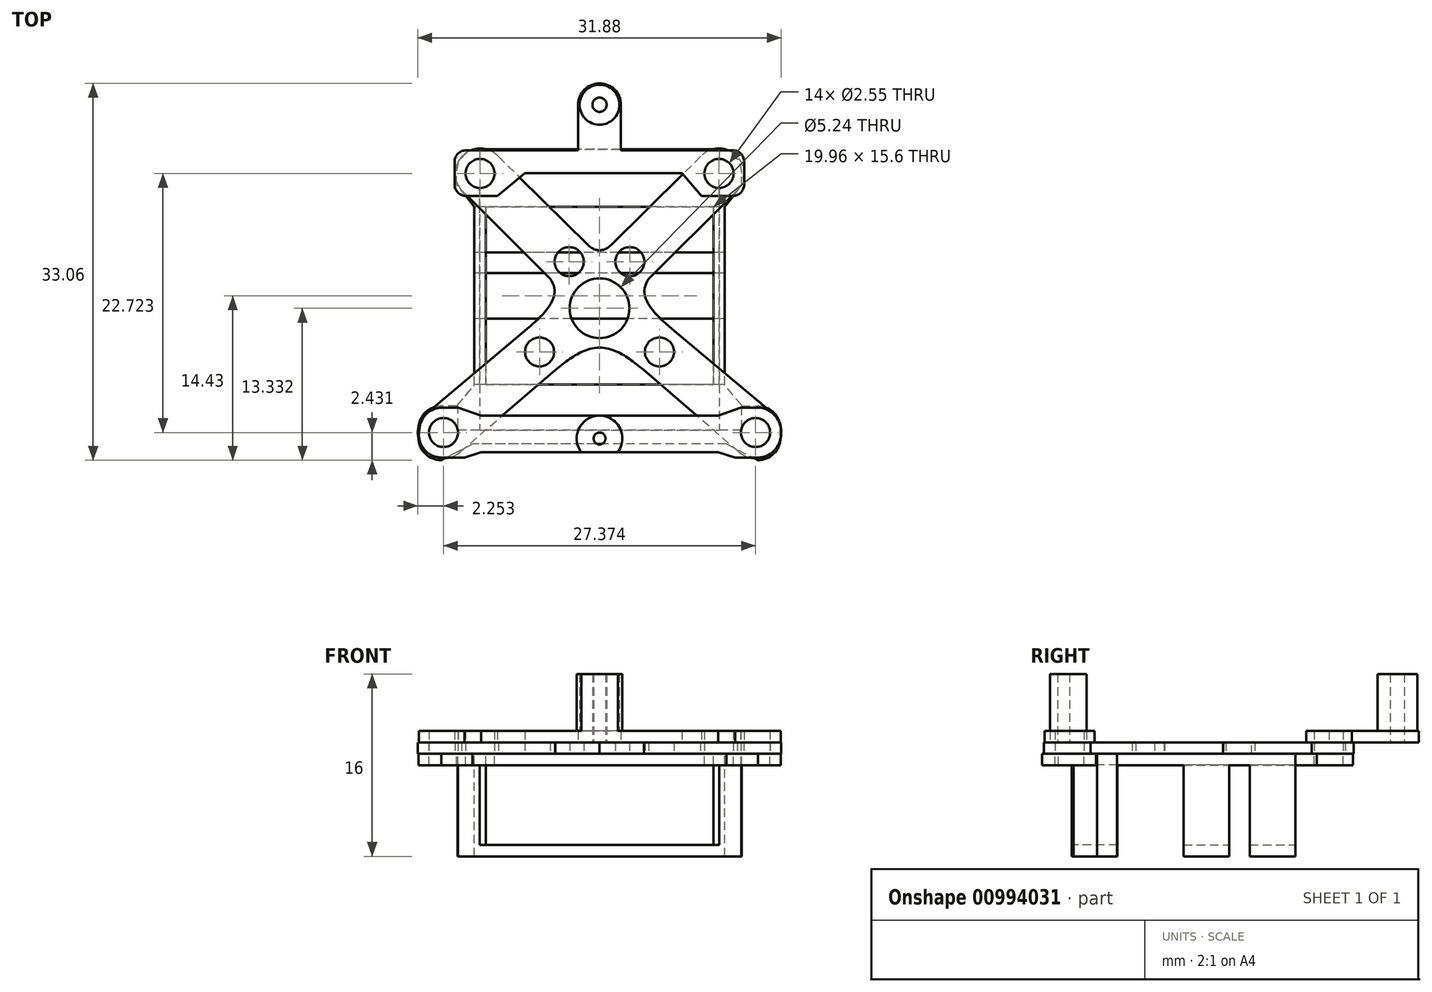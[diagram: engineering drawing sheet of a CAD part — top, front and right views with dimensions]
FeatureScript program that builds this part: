
annotation { "Feature Type Name" : "Feature", "Feature Type Description" : "" }
export const myFeature = defineFeature(function(context is Context, id is Id, definition is map)
    precondition{}
    {
        {
            var Q0;
            Q0=qCreatedBy(makeId("Top.planeOp"),FACE);
            var sketch = newSketch(context, id + "F0", { "sketchPlane" : qUnion([Q0])});
            skPoint(sketch, "E0.MirrorCS.start.orphan", {"position": v(0, 0) * mm});
            skCircle(sketch, "E1", {"center": v(-10.48, 10.72) * mm, "radius": 1.27 * mm});
            skCircle(sketch, "E2", {"center": v(-2.66, 2.99) * mm, "radius": 1.27 * mm});
            skCircle(sketch, "E3", {"center": v(-5.26, -4.93) * mm, "radius": 1.27 * mm});
            skCircle(sketch, "E4", {"center": v(-13.69, -12) * mm, "radius": 1.27 * mm});
            skLineSegment(sketch, "E5", {"start": v(-8.86, 12.2) * mm, "end": v(-1.03, 4.48) * mm});
            skLineSegment(sketch, "E6", {"start": v(-12.1, 9.24) * mm, "end": v(-4.32, 1.47) * mm});
            skArc(sketch, "E7", {"start": v(-8.86, 12.2) * mm, "mid": v(-11.96, 12.34) * mm, "end": v(-12.1, 9.24) * mm});
            skLineSegment(sketch, "E8.trimOffspring", {"start": v(-8.86, 12.2) * mm, "end": v(-8.86, 12.2) * mm});
            skLineSegment(sketch, "E9.trimOffspring", {"start": v(-12.1, 9.24) * mm, "end": v(-12.1, 9.24) * mm});
            skLineSegment(sketch, "E10", {"start": v(-12.21, -13.7) * mm, "end": v(-3.9, -6.5) * mm});
            skArc(sketch, "E11", {"start": v(-15, -10.16) * mm, "mid": v(-15.46, -13.39) * mm, "end": v(-12.21, -13.7) * mm});
            skLineSegment(sketch, "E12", {"start": v(-15, -10.16) * mm, "end": v(-6.56, -3.1) * mm});
            skFitSpline(sketch, "E13", {"points": [v(-6.56, -3.1) * mm, v(-4.32, 1.47) * mm], "startDerivative": vector(5.76, 4.8) * mm, "endDerivative": vector(-3.3, 4.4) * mm});
            skFitSpline(sketch, "E14", {"points": [v(-3.9, -6.5) * mm, v(0, -4.55) * mm], "startDerivative": vector(3.9, 2.98) * mm, "endDerivative": vector(4.87, 0.25) * mm});
            skLineSegment(sketch, "E15.MirrorCS", {"start": v(12.21, -13.7) * mm, "end": v(3.9, -6.5) * mm});
            skArc(sketch, "E16.MirrorCS", {"start": v(15, -10.16) * mm, "mid": v(15.46, -13.39) * mm, "end": v(12.21, -13.7) * mm});
            skCircle(sketch, "E17.MirrorC", {"center": v(13.69, -12) * mm, "radius": 1.27 * mm});
            skLineSegment(sketch, "E18.MirrorCS", {"start": v(15, -10.16) * mm, "end": v(6.56, -3.1) * mm});
            skFitSpline(sketch, "E19.MirrorCS", {"points": [v(3.9, -6.5) * mm, v(0, -4.55) * mm], "startDerivative": vector(-3.9, 2.98) * mm, "endDerivative": vector(-4.87, 0.25) * mm});
            skFitSpline(sketch, "E20.MirrorCS", {"points": [v(6.56, -3.1) * mm, v(4.32, 1.47) * mm], "startDerivative": vector(-5.76, 4.8) * mm, "endDerivative": vector(3.3, 4.4) * mm});
            skLineSegment(sketch, "E21.MirrorCS", {"start": v(12.1, 9.24) * mm, "end": v(4.32, 1.47) * mm});
            skCircle(sketch, "E22.MirrorC", {"center": v(2.66, 2.99) * mm, "radius": 1.27 * mm});
            skLineSegment(sketch, "E23.MirrorCS", {"start": v(8.86, 12.2) * mm, "end": v(1.03, 4.48) * mm});
            skArc(sketch, "E24.MirrorCS", {"start": v(8.86, 12.2) * mm, "mid": v(11.96, 12.34) * mm, "end": v(12.1, 9.24) * mm});
            skCircle(sketch, "E25.MirrorC", {"center": v(10.48, 10.72) * mm, "radius": 1.27 * mm});
            skCircle(sketch, "E26.MirrorC", {"center": v(5.26, -4.93) * mm, "radius": 1.27 * mm});
            skPoint(sketch, "E27.MirrorCS.start.orphan", {"position": v(1.03, 4.48) * mm});
            skFitSpline(sketch, "E28", {"points": [v(-1.03, 4.48) * mm, v(1.03, 4.48) * mm], "startDerivative": vector(1.98, -1.99) * mm, "endDerivative": vector(2, 1.99) * mm});
            skLineSegment(sketch, "E29", {"start": v(-10.48, 10.72) * mm, "end": v(-2.66, 2.99) * mm});
            skLineSegment(sketch, "E30", {"start": v(-10.48, 10.72) * mm, "end": v(-18.3, 18.46) * mm});
            skCircle(sketch, "E31", {"center": v(-18.3, 18.46) * mm, "radius": 15.5 * mm});
            skLineSegment(sketch, "E32", {"start": v(-13.69, -12) * mm, "end": v(-5.26, -4.93) * mm});
            skCircle(sketch, "E33", {"center": v(0, -1.1) * mm, "radius": 2.62 * mm});
            skSolve(sketch);
        }
        {
            var Q0;
            Q0=makeQuery(id+"F0.imprint","IMPRINT",FACE,{"disambiguationData":[TD([[makeQuery(id+"F0.imprint","IMPRINT",EDGE,{"derivedFrom":sQuery(id+"F0.wireOp",EDGE,"E1")}),-1.0]])]});
            var Q1;
            Q1=makeQuery(id+"F0.imprint","IMPRINT",FACE,{"disambiguationData":[TD([[makeQuery(id+"F0.imprint","IMPRINT",EDGE,{"derivedFrom":sQuery(id+"F0.wireOp",EDGE,"E2")}),-1.0]])]});
            extrude(context, id + "F1", {"entities" : qUnion([Q0, Q1]), "depth" : 1 * mm, "offsetDistance" : 25 * mm});
        }
        {
            var Q0;
            Q0=qCreatedBy(makeId("Top.planeOp"),FACE);
            var sketch = newSketch(context, id + "F2", { "sketchPlane" : qUnion([Q0])});
            skLineSegment(sketch, "E34.bottom", {"start": v(11.14, -13) * mm, "end": v(-11.14, -13) * mm});
            skLineSegment(sketch, "E34.top", {"start": v(10.46, 12.85) * mm, "end": v(-10.54, 12.85) * mm});
            skLineSegment(sketch, "E34.left", {"start": v(12.46, -9.68) * mm, "end": v(12.46, -9.59) * mm});
            skLineSegment(sketch, "E34.right", {"start": v(-12.54, 9.76) * mm, "end": v(-12.54, 10.85) * mm});
            skPoint(sketch, "E34.middle", {"position": v(0, 0) * mm});
            skLineSegment(sketch, "E35.top", {"start": v(-12.54, -9.68) * mm, "end": v(-13.89, -9.68) * mm});
            skLineSegment(sketch, "E35.right", {"start": v(-15.89, -12.43) * mm, "end": v(-15.89, -11.68) * mm});
            skLineSegment(sketch, "E36.MirrorCS", {"start": v(15.89, -12.43) * mm, "end": v(15.89, -11.68) * mm});
            skLineSegment(sketch, "E37.MirrorCS", {"start": v(12.46, -9.68) * mm, "end": v(13.89, -9.68) * mm});
            skLineSegment(sketch, "E38.bottom", {"start": v(9.98, -7.8) * mm, "end": v(-9.98, -7.8) * mm});
            skLineSegment(sketch, "E38.top", {"start": v(9.98, 7.8) * mm, "end": v(-9.98, 7.8) * mm});
            skLineSegment(sketch, "E38.left", {"start": v(9.98, -7.8) * mm, "end": v(9.98, 7.8) * mm});
            skLineSegment(sketch, "E38.right", {"start": v(-9.98, -7.8) * mm, "end": v(-9.98, 7.8) * mm});
            skPoint(sketch, "E39.visualSharp", {"position": v(-12.54, 12.85) * mm});
            skArc(sketch, "E39.filletArc", {"start": v(-10.54, 12.85) * mm, "mid": v(-11.95, 12.26) * mm, "end": v(-12.54, 10.85) * mm});
            skPoint(sketch, "E40.visualSharp", {"position": v(12.46, 12.85) * mm});
            skArc(sketch, "E40.filletArc", {"start": v(12.46, 10.85) * mm, "mid": v(11.88, 12.26) * mm, "end": v(10.46, 12.85) * mm});
            skPoint(sketch, "E41.visualSharp", {"position": v(-15.89, -9.68) * mm});
            skArc(sketch, "E41.filletArc", {"start": v(-13.89, -9.68) * mm, "mid": v(-15.3, -10.26) * mm, "end": v(-15.89, -11.68) * mm});
            skPoint(sketch, "E42.visualSharp", {"position": v(-15.89, -14.43) * mm});
            skArc(sketch, "E42.filletArc", {"start": v(-15.89, -12.43) * mm, "mid": v(-15.3, -13.84) * mm, "end": v(-13.89, -14.43) * mm});
            skPoint(sketch, "E43.visualSharp", {"position": v(15.89, -9.68) * mm});
            skArc(sketch, "E43.filletArc", {"start": v(15.89, -11.68) * mm, "mid": v(15.3, -10.26) * mm, "end": v(13.89, -9.68) * mm});
            skPoint(sketch, "E44.visualSharp", {"position": v(15.89, -14.43) * mm});
            skArc(sketch, "E44.filletArc", {"start": v(13.89, -14.43) * mm, "mid": v(15.3, -13.84) * mm, "end": v(15.89, -12.43) * mm});
            skLineSegment(sketch, "E45", {"start": v(-12.54, -9.68) * mm, "end": v(-10.98, -7.84) * mm});
            skLineSegment(sketch, "E46", {"start": v(-10.98, -7.84) * mm, "end": v(-10.98, 7.8) * mm});
            skLineSegment(sketch, "E47", {"start": v(-10.98, 7.8) * mm, "end": v(-12.54, 9.76) * mm});
            skLineSegment(sketch, "E48", {"start": v(-13.89, -14.43) * mm, "end": v(-11.14, -13) * mm});
            skLineSegment(sketch, "E49", {"start": v(11.14, -13) * mm, "end": v(13.89, -14.43) * mm});
            skLineSegment(sketch, "E50.MirrorCS", {"start": v(10.98, 7.8) * mm, "end": v(12.54, 9.76) * mm});
            skLineSegment(sketch, "E51.MirrorCS", {"start": v(10.98, -7.84) * mm, "end": v(10.98, 7.8) * mm});
            skLineSegment(sketch, "E52.MirrorCS", {"start": v(12.54, -9.68) * mm, "end": v(10.98, -7.84) * mm});
            skLineSegment(sketch, "E53.trimOffspring", {"start": v(12.46, 9.67) * mm, "end": v(12.46, 10.85) * mm});
            skSolve(sketch);
        }
        {
            var Q0;
            Q0=makeQuery(id+"F2.imprint","IMPRINT",FACE,{"disambiguationData":[TD([[makeQuery(id+"F2.imprint","IMPRINT",EDGE,{"derivedFrom":sQuery(id+"F2.wireOp",EDGE,"E34.bottom")}),-1.0]])]});
            extrude(context, id + "F3", {"entities" : qUnion([Q0]), "oppositeDirection" : true, "depth" : 1 * mm, "offsetDistance" : 25 * mm});
        }
        {
            var Q0;
            Q0=makeQuery(id+"F3.opExtrude","CAP_FACE",FACE,{"disambiguationData":[OSD([sQuery(id+"F2.wireOp",EDGE,"E34.bottom"),sQuery(id+"F2.wireOp",EDGE,"E34.top"),sQuery(id+"F2.wireOp",EDGE,"E34.left"),sQuery(id+"F2.wireOp",EDGE,"E34.right"),sQuery(id+"F2.wireOp",EDGE,"E35.bottom"),sQuery(id+"F2.wireOp",EDGE,"E35.top"),sQuery(id+"F2.wireOp",EDGE,"E35.left"),sQuery(id+"F2.wireOp",EDGE,"E35.right"),sQuery(id+"F2.wireOp",EDGE,"58bdf640-9ded-4e14-aef3-7ecadc54e6020.MirrorCS"),sQuery(id+"F2.wireOp",EDGE,"8ba404dc-4aa1-4afc-8ac7-2d9d7d40b4e10.MirrorCS"),sQuery(id+"F2.wireOp",EDGE,"E36.MirrorCS"),sQuery(id+"F2.wireOp",EDGE,"E37.MirrorCS"),sQuery(id+"F2.wireOp",EDGE,"E38.bottom"),sQuery(id+"F2.wireOp",EDGE,"E38.top"),sQuery(id+"F2.wireOp",EDGE,"E38.left"),sQuery(id+"F2.wireOp",EDGE,"E38.right")])],"isStart":false});
            var sketch = newSketch(context, id + "F4", { "sketchPlane" : qUnion([Q0])});
            skLineSegment(sketch, "E54.bottom", {"start": v(12.46, 7.8) * mm, "end": v(-12.46, 7.8) * mm});
            skLineSegment(sketch, "E54.top", {"start": v(12.46, 11.8) * mm, "end": v(-12.46, 11.8) * mm});
            skLineSegment(sketch, "E54.left", {"start": v(12.46, 7.8) * mm, "end": v(12.46, 11.8) * mm});
            skLineSegment(sketch, "E54.right", {"start": v(-12.46, 7.8) * mm, "end": v(-12.46, 11.8) * mm});
            skPoint(sketch, "E54.middle", {"position": v(0, 9.8) * mm});
            skLineSegment(sketch, "E55.bottom", {"start": v(12.46, -2) * mm, "end": v(-12.46, -2) * mm});
            skLineSegment(sketch, "E55.top", {"start": v(12.46, 2) * mm, "end": v(-12.46, 2) * mm});
            skLineSegment(sketch, "E55.left", {"start": v(12.46, -2) * mm, "end": v(12.46, 2) * mm});
            skLineSegment(sketch, "E55.right", {"start": v(-12.46, -2) * mm, "end": v(-12.46, 2) * mm});
            skPoint(sketch, "E55.middle", {"position": v(0, 0) * mm});
            skLineSegment(sketch, "E56.bottom", {"start": v(12.46, -7.8) * mm, "end": v(-12.46, -7.8) * mm});
            skLineSegment(sketch, "E56.top", {"start": v(12.46, -3.8) * mm, "end": v(-12.46, -3.8) * mm});
            skLineSegment(sketch, "E56.left", {"start": v(12.46, -7.8) * mm, "end": v(12.46, -3.8) * mm});
            skLineSegment(sketch, "E56.right", {"start": v(-12.46, -7.8) * mm, "end": v(-12.46, -3.8) * mm});
            skPoint(sketch, "E56.middle", {"position": v(0, -5.8) * mm});
            skPoint(sketch, "E56.middle.positionSnap0", {"position": v(0, -7.8) * mm});
            skPoint(sketch, "E56.centerSnap0", {"position": v(0, -7.8) * mm});
            skSolve(sketch);
        }
        {
            var Q0;
            {var subQ5=sQuery(id+"F4.wireOp",EDGE,"E54.top");Q0=makeQuery(id+"F4.imprint","IMPRINT",FACE,{"disambiguationData":[TD([[makeQuery(id+"F4.imprint","IMPRINT",EDGE,{"derivedFrom":subQ5}),1.0]])]});}
            var Q1;
            {var subQ0=sQuery(id+"F4.wireOp",EDGE,"E55.bottom");var subQ1=makeQuery(id+"F3.opExtrude","CAP_EDGE",EDGE,{"disambiguationData":[OSD([sQuery(id+"F2.wireOp",EDGE,"E38.left")])],"isStart":false});var subQ2=makeQuery(id+"F4.imprint","INTERSECT",VERTEX,{"derivedFrom":[subQ1,subQ0]});Q1=makeQuery(id+"F4.imprint","IMPRINT",FACE,{"disambiguationData":[TD([[makeQuery(id+"F4.imprint","IMPRINT",EDGE,{"disambiguationData":[TD([[subQ2,-1.0]])],"derivedFrom":subQ0}),-1.0]])]});}
            var Q2;
            {var subQ0=sQuery(id+"F4.wireOp",EDGE,"E56.bottom");var subQ1=makeQuery(id+"F3.opExtrude","CAP_EDGE",EDGE,{"disambiguationData":[OSD([sQuery(id+"F2.wireOp",EDGE,"E38.left")])],"isStart":false});var subQ2=makeQuery(id+"F4.imprint","INTERSECT",VERTEX,{"derivedFrom":[subQ1,subQ0]});Q2=makeQuery(id+"F4.imprint","IMPRINT",FACE,{"disambiguationData":[TD([[makeQuery(id+"F4.imprint","IMPRINT",EDGE,{"disambiguationData":[TD([[subQ2,-1.0]])],"derivedFrom":subQ0}),-1.0]])]});}
            extrude(context, id + "F5", {"entities" : qUnion([Q0, Q1, Q2]), "operationType" : NewBodyOperationType.ADD, "depth" : 8 * mm, "offsetDistance" : 25 * mm});
        }
        {
            var Q0;
            Q0=makeQuery(id+"F5.opExtrude","SWEPT_FACE",FACE,{"disambiguationData":[OSD([sQuery(id+"F4.wireOp",EDGE,"E54.top")])]});
            var sketch = newSketch(context, id + "F6", { "sketchPlane" : qUnion([Q0])});
            skLineSegment(sketch, "E57.bottom", {"start": v(10.5, -0.97) * mm, "end": v(-10.5, -0.97) * mm});
            skLineSegment(sketch, "E57.top", {"start": v(10.5, -9) * mm, "end": v(-10.5, -9) * mm});
            skPoint(sketch, "E57.middle", {"position": v(0, -4.75) * mm});
            skPoint(sketch, "E57.middle.positionSnap0", {"position": v(0, -9) * mm});
            skPoint(sketch, "E57.centerSnap0", {"position": v(0, -9) * mm});
            skLineSegment(sketch, "E58", {"start": v(-10.5, -8) * mm, "end": v(-10.5, -0.97) * mm});
            skLineSegment(sketch, "E59", {"start": v(10.5, -8) * mm, "end": v(10.5, -0.97) * mm});
            skLineSegment(sketch, "E60", {"start": v(-10.5, -8) * mm, "end": v(10.5, -8) * mm});
            skSolve(sketch);
        }
        {
            var Q0;
            Q0 = qSketchRegion(id + "F6", true);
            extrude(context, id + "F7", {"entities" : qUnion([Q0]), "operationType" : NewBodyOperationType.REMOVE, "oppositeDirection" : true, "depth" : 25 * mm, "offsetDistance" : 25 * mm});
        }
        {
            var Q0;
            Q0=makeQuery(id+"F1.opExtrude","CAP_FACE",FACE,{"disambiguationData":[OSD([sQuery(id+"F0.wireOp",EDGE,"E1"),sQuery(id+"F0.wireOp",EDGE,"E2"),sQuery(id+"F0.wireOp",EDGE,"E3"),sQuery(id+"F0.wireOp",EDGE,"E4"),sQuery(id+"F0.wireOp",EDGE,"E5"),sQuery(id+"F0.wireOp",EDGE,"E6"),sQuery(id+"F0.wireOp",EDGE,"E7"),sQuery(id+"F0.wireOp",EDGE,"E10"),sQuery(id+"F0.wireOp",EDGE,"E11"),sQuery(id+"F0.wireOp",EDGE,"E12"),sQuery(id+"F0.wireOp",EDGE,"E13"),sQuery(id+"F0.wireOp",EDGE,"E14"),sQuery(id+"F0.wireOp",EDGE,"E15.MirrorCS"),sQuery(id+"F0.wireOp",EDGE,"E16.MirrorCS"),sQuery(id+"F0.wireOp",EDGE,"E17.MirrorC"),sQuery(id+"F0.wireOp",EDGE,"E18.MirrorCS"),sQuery(id+"F0.wireOp",EDGE,"E19.MirrorCS"),sQuery(id+"F0.wireOp",EDGE,"E20.MirrorCS"),sQuery(id+"F0.wireOp",EDGE,"E21.MirrorCS"),sQuery(id+"F0.wireOp",EDGE,"E22.MirrorC"),sQuery(id+"F0.wireOp",EDGE,"E23.MirrorCS"),sQuery(id+"F0.wireOp",EDGE,"E24.MirrorCS"),sQuery(id+"F0.wireOp",EDGE,"E25.MirrorC"),sQuery(id+"F0.wireOp",EDGE,"E26.MirrorC"),sQuery(id+"F0.wireOp",EDGE,"E28")])],"isStart":false});
            cPlane(context, id + "F8", {"entities" : qUnion([Q0]), "cplaneType" : CPlaneType.OFFSET, "offset" : 0 * mm, "width" : 150 * mm, "height" : 150 * mm});
        }
        {
            var Q0;
            Q0=qCreatedBy(id+"F8.planeOp",FACE);
            var Q1;
            Q1=qCreatedBy(id+"F8.planeOp",FACE);
            var Q2;
            Q2=qCreatedBy(id+"F8.planeOp",FACE);
            var Q3;
            Q3=qCreatedBy(id+"F8.planeOp",FACE);
            var sketch = newSketch(context, id + "F9", { "sketchPlane" : qUnion([Q0, Q1, Q2, Q3])});
            skLineSegment(sketch, "E61", {"start": v(-13.81, -9.83) * mm, "end": v(-12.39, -9.83) * mm});
            skLineSegment(sketch, "E62", {"start": v(15.9, -11.83) * mm, "end": v(15.9, -12.2) * mm});
            skLineSegment(sketch, "E63", {"start": v(13.9, -14.2) * mm, "end": v(11.91, -14.2) * mm});
            skLineSegment(sketch, "E64", {"start": v(-15.84, -11.96) * mm, "end": v(-15.8, -11.6) * mm});
            skCircle(sketch, "E65", {"center": v(0, -12.52) * mm, "radius": 2 * mm});
            skCircle(sketch, "E66", {"center": v(0, -12.52) * mm, "radius": 0.53 * mm});
            skPoint(sketch, "E67.visualSharp", {"position": v(-15.59, -9.83) * mm});
            skArc(sketch, "E67.filletArc", {"start": v(-13.81, -9.83) * mm, "mid": v(-15.14, -10.33) * mm, "end": v(-15.8, -11.6) * mm});
            skPoint(sketch, "E68.visualSharp", {"position": v(-16.1, -14.2) * mm});
            skArc(sketch, "E68.filletArc", {"start": v(-15.84, -11.96) * mm, "mid": v(-15.35, -13.53) * mm, "end": v(-13.85, -14.2) * mm});
            skPoint(sketch, "E69.visualSharp", {"position": v(15.9, -9.83) * mm});
            skArc(sketch, "E69.filletArc", {"start": v(15.9, -11.83) * mm, "mid": v(15.31, -10.41) * mm, "end": v(13.9, -9.83) * mm});
            skPoint(sketch, "E70.visualSharp", {"position": v(15.9, -14.2) * mm});
            skArc(sketch, "E70.filletArc", {"start": v(13.9, -14.2) * mm, "mid": v(15.31, -13.61) * mm, "end": v(15.9, -12.2) * mm});
            skLineSegment(sketch, "E71", {"start": v(-12.39, -9.83) * mm, "end": v(-10.4, -10.52) * mm});
            skLineSegment(sketch, "E72", {"start": v(-10.4, -10.52) * mm, "end": v(0, -10.52) * mm});
            skLineSegment(sketch, "E73.MirrorCS", {"start": v(12.39, -9.83) * mm, "end": v(10.4, -10.52) * mm});
            skLineSegment(sketch, "E74.MirrorCS", {"start": v(10.4, -10.52) * mm, "end": v(0, -10.52) * mm});
            skLineSegment(sketch, "E75.trimOffspring", {"start": v(12.39, -9.83) * mm, "end": v(13.9, -9.83) * mm});
            skLineSegment(sketch, "E76", {"start": v(-11.84, -14.2) * mm, "end": v(-10.4, -13.72) * mm});
            skLineSegment(sketch, "E77", {"start": v(-10.4, -13.72) * mm, "end": v(0, -13.72) * mm});
            skLineSegment(sketch, "E78", {"start": v(0, -13.72) * mm, "end": v(10.4, -13.72) * mm});
            skLineSegment(sketch, "E79", {"start": v(10.4, -13.72) * mm, "end": v(11.91, -14.2) * mm});
            skLineSegment(sketch, "E80.trimOffspring", {"start": v(-11.84, -14.2) * mm, "end": v(-13.85, -14.2) * mm});
            skSolve(sketch);
        }
        {
            var Q0;
            Q0=qCreatedBy(id+"F8.planeOp",FACE);
            var sketch = newSketch(context, id + "F10", { "sketchPlane" : qUnion([Q0])});
            skLineSegment(sketch, "E81.bottom", {"start": v(-11.71, 12.75) * mm, "end": v(-1.88, 12.75) * mm});
            skLineSegment(sketch, "E81.top", {"start": v(-11.71, 8.75) * mm, "end": v(-8.96, 8.75) * mm});
            skLineSegment(sketch, "E81.left", {"start": v(-12.71, 11.75) * mm, "end": v(-12.71, 9.75) * mm});
            skLineSegment(sketch, "E81.right", {"start": v(12.69, 11.75) * mm, "end": v(12.69, 9.75) * mm});
            skArc(sketch, "E82", {"start": v(1.88, 16.75) * mm, "mid": v(0, 18.63) * mm, "end": v(-1.88, 16.75) * mm});
            skLineSegment(sketch, "E83", {"start": v(-1.88, 16.75) * mm, "end": v(-1.88, 12.75) * mm});
            skLineSegment(sketch, "E84", {"start": v(1.88, 16.75) * mm, "end": v(1.88, 12.75) * mm});
            skLineSegment(sketch, "E85.trimOffspring", {"start": v(1.88, 12.75) * mm, "end": v(11.69, 12.75) * mm});
            skCircle(sketch, "E86", {"center": v(0, 16.75) * mm, "radius": 0.62 * mm});
            skCircle(sketch, "E87", {"center": v(0, 16.75) * mm, "radius": 1.75 * mm});
            skPoint(sketch, "E88.visualSharp", {"position": v(-12.71, 12.75) * mm});
            skArc(sketch, "E88.filletArc", {"start": v(-11.71, 12.75) * mm, "mid": v(-12.42, 12.46) * mm, "end": v(-12.71, 11.75) * mm});
            skPoint(sketch, "E89.visualSharp", {"position": v(12.69, 12.75) * mm});
            skArc(sketch, "E89.filletArc", {"start": v(12.69, 11.75) * mm, "mid": v(12.4, 12.46) * mm, "end": v(11.69, 12.75) * mm});
            skPoint(sketch, "E90.visualSharp", {"position": v(-12.71, 8.75) * mm});
            skArc(sketch, "E90.filletArc", {"start": v(-12.71, 9.75) * mm, "mid": v(-12.42, 9.05) * mm, "end": v(-11.71, 8.75) * mm});
            skPoint(sketch, "E91.visualSharp", {"position": v(12.69, 8.75) * mm});
            skArc(sketch, "E91.filletArc", {"start": v(11.69, 8.75) * mm, "mid": v(12.4, 9.05) * mm, "end": v(12.69, 9.75) * mm});
            skLineSegment(sketch, "E92", {"start": v(-8.96, 8.75) * mm, "end": v(-6.55, 10.75) * mm});
            skLineSegment(sketch, "E93", {"start": v(-6.55, 10.75) * mm, "end": v(7.22, 10.75) * mm});
            skLineSegment(sketch, "E94", {"start": v(7.22, 10.75) * mm, "end": v(8.94, 8.75) * mm});
            skLineSegment(sketch, "E95.trimOffspring", {"start": v(8.94, 8.75) * mm, "end": v(11.69, 8.75) * mm});
            skSolve(sketch);
        }
        {
            var Q0;
            Q0=makeQuery(id+"F9.imprint","IMPRINT",FACE,{"disambiguationData":[TD([[makeQuery(id+"F9.imprint","IMPRINT",EDGE,{"derivedFrom":sQuery(id+"F9.wireOp",EDGE,"E61")}),-1.0]])]});
            var Q1;
            Q1=makeQuery(id+"F10.imprint","IMPRINT",FACE,{"disambiguationData":[TD([[makeQuery(id+"F10.imprint","IMPRINT",EDGE,{"derivedFrom":sQuery(id+"F10.wireOp",EDGE,"E81.bottom")}),-1.0]])]});
            var Q2;
            Q2=makeQuery(id+"F9.imprint","IMPRINT",FACE,{"disambiguationData":[TD([[makeQuery(id+"F9.imprint","IMPRINT",EDGE,{"derivedFrom":sQuery(id+"F9.wireOp",EDGE,"E62")}),-1.0]])]});
            extrude(context, id + "F11", {"entities" : qUnion([Q0, Q1, Q2]), "depth" : 1 * mm, "offsetDistance" : 25 * mm});
        }
        {
            var Q0;
            Q0=sQuery(id+"F0.wireOp",VERTEX,"E32.start");
            var Q1;
            Q1=sQuery(id+"F0.wireOp",VERTEX,"E16.MirrorCS.center");
            var Q2;
            Q2=sQuery(id+"F0.wireOp",VERTEX,"E24.MirrorCS.center");
            var Q3;
            Q3=sQuery(id+"F0.wireOp",VERTEX,"E29.start");
            var Q4;
            Q4=makeQuery(id+"F3.opExtrude","SWEPT_BODY",BODY,{"disambiguationData":[OSD([sQuery(id+"F2.wireOp",EDGE,"E34.bottom"),sQuery(id+"F2.wireOp",EDGE,"E34.top"),sQuery(id+"F2.wireOp",EDGE,"E34.left"),sQuery(id+"F2.wireOp",EDGE,"E34.right"),sQuery(id+"F2.wireOp",EDGE,"E35.bottom"),sQuery(id+"F2.wireOp",EDGE,"E35.top"),sQuery(id+"F2.wireOp",EDGE,"E35.left"),sQuery(id+"F2.wireOp",EDGE,"E35.right"),sQuery(id+"F2.wireOp",EDGE,"58bdf640-9ded-4e14-aef3-7ecadc54e6020.MirrorCS"),sQuery(id+"F2.wireOp",EDGE,"8ba404dc-4aa1-4afc-8ac7-2d9d7d40b4e10.MirrorCS"),sQuery(id+"F2.wireOp",EDGE,"E36.MirrorCS"),sQuery(id+"F2.wireOp",EDGE,"E37.MirrorCS"),sQuery(id+"F2.wireOp",EDGE,"E38.bottom"),sQuery(id+"F2.wireOp",EDGE,"E38.top"),sQuery(id+"F2.wireOp",EDGE,"E38.left"),sQuery(id+"F2.wireOp",EDGE,"E38.right")])]});
            var Q5;
            Q5=makeQuery(id+"F11.opExtrude","SWEPT_BODY",BODY,{"disambiguationData":[OSD([sQuery(id+"F9.wireOp",EDGE,"E61"),sQuery(id+"F9.wireOp",EDGE,"E62"),sQuery(id+"F9.wireOp",EDGE,"E63"),sQuery(id+"F9.wireOp",EDGE,"E64")])]});
            hole(context, id + "F12", {"style" : HoleStyle.SIMPLE, "endStyle" : HoleEndStyle.THROUGH, "holeDiameter" : 2.55 * mm, "majorDiameter" : 5 * mm, "isTappedThrough" : true, "tappedDepth" : 12 * mm, "tapClearance" : 3, "startFromSketch" : true, "locations" : qUnion([Q0, Q1, Q2, Q3]), "scope" : qUnion([Q4, Q5])});
        }
        {
            var Q0;
            Q0=sQuery(id+"F0.wireOp",VERTEX,"E32.start");
            var Q1;
            Q1=sQuery(id+"F0.wireOp",VERTEX,"E16.MirrorCS.center");
            var Q2;
            Q2=sQuery(id+"F0.wireOp",VERTEX,"E29.start");
            var Q3;
            Q3=sQuery(id+"F0.wireOp",VERTEX,"E24.MirrorCS.center");
            var Q4;
            Q4=makeQuery(id+"F11.opExtrude","SWEPT_BODY",BODY,{"disambiguationData":[OSD([sQuery(id+"F9.wireOp",EDGE,"E61"),sQuery(id+"F9.wireOp",EDGE,"E62"),sQuery(id+"F9.wireOp",EDGE,"E63"),sQuery(id+"F9.wireOp",EDGE,"E64")])]});
            var Q5;
            Q5=makeQuery(id+"F11.opExtrude","SWEPT_BODY",BODY,{"disambiguationData":[OSD([sQuery(id+"F9.wireOp",EDGE,"E61"),sQuery(id+"F9.wireOp",EDGE,"E62"),sQuery(id+"F9.wireOp",EDGE,"E63"),sQuery(id+"F9.wireOp",EDGE,"E64")])]});
            var Q6;
            Q6=makeQuery(id+"F11.opExtrude","SWEPT_BODY",BODY,{"disambiguationData":[OSD([sQuery(id+"F10.wireOp",EDGE,"E81.bottom"),sQuery(id+"F10.wireOp",EDGE,"E81.top"),sQuery(id+"F10.wireOp",EDGE,"E81.left"),sQuery(id+"F10.wireOp",EDGE,"E81.right"),sQuery(id+"F10.wireOp",EDGE,"E82"),sQuery(id+"F10.wireOp",EDGE,"E83"),sQuery(id+"F10.wireOp",EDGE,"E84"),sQuery(id+"F10.wireOp",EDGE,"E85.trimOffspring"),sQuery(id+"F10.wireOp",EDGE,"E86")])]});
            hole(context, id + "F13", {"style" : HoleStyle.SIMPLE, "endStyle" : HoleEndStyle.THROUGH, "oppositeDirection" : true, "holeDiameter" : 2.55 * mm, "majorDiameter" : 5 * mm, "isTappedThrough" : true, "tappedDepth" : 12 * mm, "tapClearance" : 3, "startFromSketch" : true, "locations" : qUnion([Q0, Q1, Q2, Q3]), "scope" : qUnion([Q4, Q5, Q6])});
        }
        {
            var Q0;
            Q0=makeQuery(id+"F9.imprint","IMPRINT",FACE,{"disambiguationData":[TD([[makeQuery(id+"F9.imprint","IMPRINT",EDGE,{"derivedFrom":sQuery(id+"F9.wireOp",EDGE,"E66")}),-1.0]])]});
            var Q1;
            {var subQ0=sQuery(id+"F9.wireOp",EDGE,"E65");var subQ1=sQuery(id+"F9.wireOp",EDGE,"E63");var subQ2=makeQuery(id+"F9.imprint","INTERSECT",VERTEX,{"disambiguationData":[OD(0.0)],"derivedFrom":[subQ1,subQ0]});Q1=makeQuery(id+"F9.imprint","IMPRINT",FACE,{"disambiguationData":[TD([[makeQuery(id+"F9.imprint","IMPRINT",EDGE,{"disambiguationData":[TD([[subQ2,-1.0]])],"derivedFrom":subQ1}),1.0]])]});}
            var Q2;
            Q2=makeQuery(id+"F10.imprint","IMPRINT",FACE,{"disambiguationData":[TD([[makeQuery(id+"F10.imprint","IMPRINT",EDGE,{"derivedFrom":sQuery(id+"F10.wireOp",EDGE,"E86")}),-1.0]])]});
            var Q3;
            Q3=sQuery(id+"F9.wireOp",EDGE,"E65");
            extrude(context, id + "F14", {"entities" : qUnion([Q0, Q1, Q2]), "operationType" : NewBodyOperationType.ADD, "surfaceEntities" : qUnion([Q3]), "depth" : 6 * mm, "offsetDistance" : 25 * mm});
        }
        {
            var Q0;
            {var subQ3=makeQuery(id+"F3.opExtrude","CAP_EDGE",EDGE,{"disambiguationData":[OSD([sQuery(id+"F2.wireOp",EDGE,"E51.MirrorCS")])],"isStart":false});var subQ5=sQuery(id+"F4.wireOp",EDGE,"E56.top");var subQ6=makeQuery(id+"F4.imprint","INTERSECT",VERTEX,{"derivedFrom":[subQ3,subQ5]});Q0=makeQuery(id+"F4.imprint","IMPRINT",FACE,{"disambiguationData":[TD([[makeQuery(id+"F4.imprint","IMPRINT",EDGE,{"disambiguationData":[TD([[subQ6,-1.0]])],"derivedFrom":subQ5}),1.0]])]});}
            var Q1;
            {var subQ0=sQuery(id+"F4.wireOp",EDGE,"E55.bottom");var subQ1=makeQuery(id+"F3.opExtrude","CAP_EDGE",EDGE,{"disambiguationData":[OSD([sQuery(id+"F2.wireOp",EDGE,"E51.MirrorCS")])],"isStart":false});var subQ2=makeQuery(id+"F4.imprint","INTERSECT",VERTEX,{"derivedFrom":[subQ1,subQ0]});Q1=makeQuery(id+"F4.imprint","IMPRINT",FACE,{"disambiguationData":[TD([[makeQuery(id+"F4.imprint","IMPRINT",EDGE,{"disambiguationData":[TD([[subQ2,-1.0]])],"derivedFrom":subQ0}),-1.0]])]});}
            var Q2;
            {var subQ0=sQuery(id+"F4.wireOp",EDGE,"E55.bottom");var subQ1=makeQuery(id+"F3.opExtrude","CAP_EDGE",EDGE,{"disambiguationData":[OSD([sQuery(id+"F2.wireOp",EDGE,"E46")])],"isStart":false});var subQ2=makeQuery(id+"F4.imprint","INTERSECT",VERTEX,{"derivedFrom":[subQ1,subQ0]});Q2=makeQuery(id+"F4.imprint","IMPRINT",FACE,{"disambiguationData":[TD([[makeQuery(id+"F4.imprint","IMPRINT",EDGE,{"disambiguationData":[TD([[subQ2,1.0]])],"derivedFrom":subQ0}),-1.0]])]});}
            var Q3;
            {var subQ3=makeQuery(id+"F3.opExtrude","CAP_EDGE",EDGE,{"disambiguationData":[OSD([sQuery(id+"F2.wireOp",EDGE,"E46")])],"isStart":false});var subQ5=sQuery(id+"F4.wireOp",EDGE,"E56.top");var subQ6=makeQuery(id+"F4.imprint","INTERSECT",VERTEX,{"derivedFrom":[subQ3,subQ5]});Q3=makeQuery(id+"F4.imprint","IMPRINT",FACE,{"disambiguationData":[TD([[makeQuery(id+"F4.imprint","IMPRINT",EDGE,{"disambiguationData":[TD([[subQ6,1.0]])],"derivedFrom":subQ5}),1.0]])]});}
            extrude(context, id + "F15", {"entities" : qUnion([Q0, Q1, Q2, Q3]), "operationType" : NewBodyOperationType.ADD, "depth" : 8 * mm, "offsetDistance" : 25 * mm});
        }
    });
